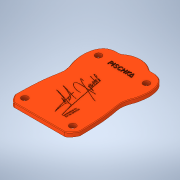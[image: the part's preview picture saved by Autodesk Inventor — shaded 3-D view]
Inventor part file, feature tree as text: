
AUTODESK INVENTOR PART (.ipt)
format: ipt  version: 2020.1 (Build 241239000, 239)  size: 2,903,040 bytes
history: native  units: mm
features: sketch x4, extrude x2, emboss x2, chamfer x1
ambient origin geometry x8: Origin, YZ Plane, XZ Plane, XY Plane, X Axis, Y Axis, Z Axis, Center Point
bodies: Solid1 (feature_tree)
feature tree (9):
  extrude  "Extrusion1"  Depth=0.5mm TaperAngle=0.0deg
  sketch  "Sketch2"  dims[d28=0.5mm d29=2.0mm d30=45.0deg d31=0.8mm d32=0.0mm d33=0.7mm d34=0.0mm]
  extrude  "Extrusion3"  Depth=0.7mm TaperAngle=0.0deg
  chamfer  "Chamfer1"  Distance=0.7mm
  emboss  "Emboss2"
  emboss  "Emboss3"
  sketch  "Sketch1"  dims[d0=3.5mm d1=0.0mm d26=0.5mm d27=0.0mm]
  sketch  "Sketch4"  dims[d35=0.5mm]
  sketch  "Sketch5"  dims[d36=0.872665mm d37=0.5mm d38=0.872665mm]
